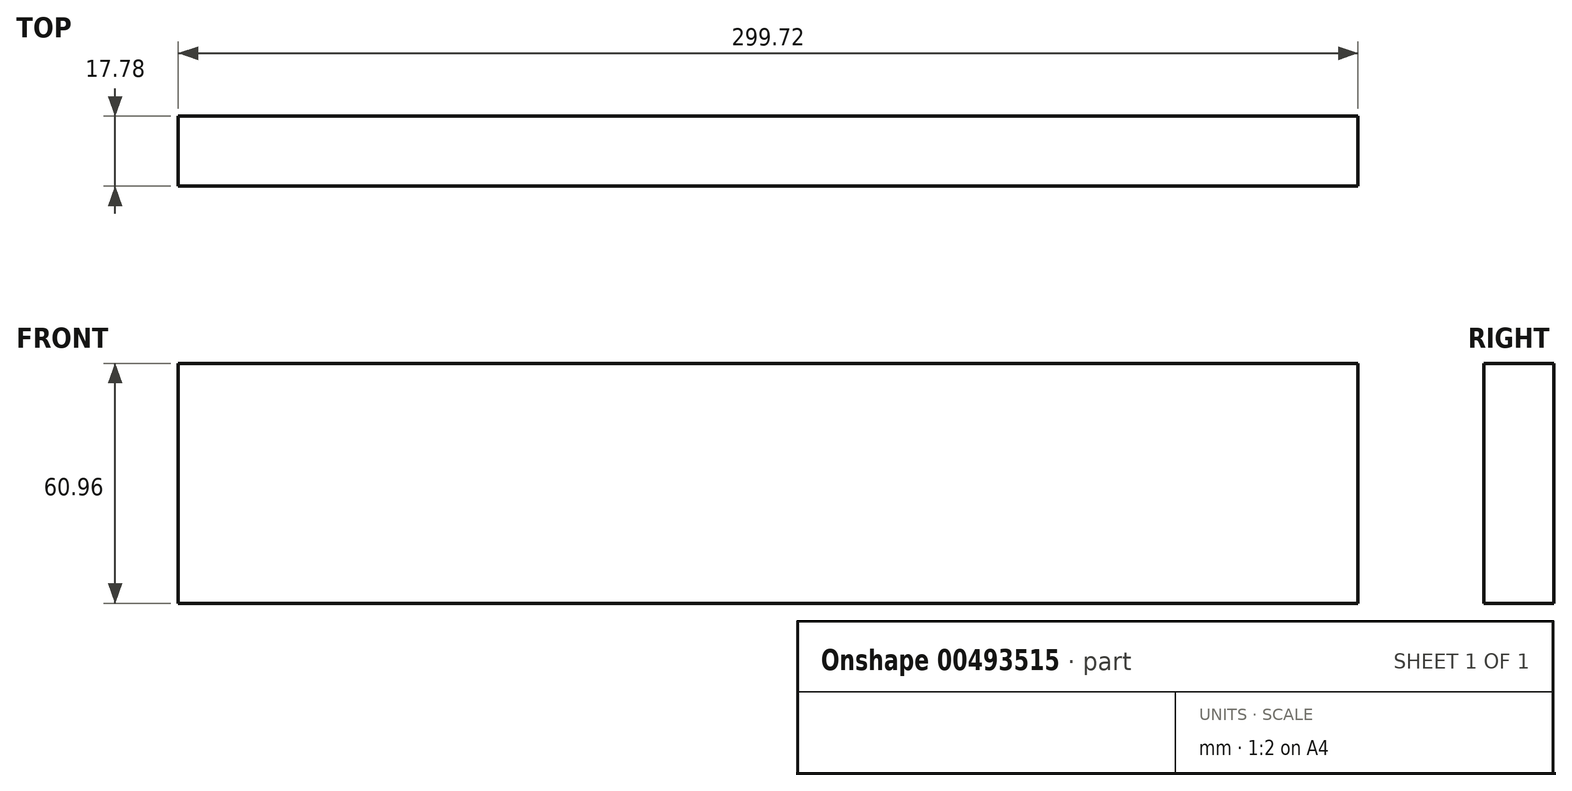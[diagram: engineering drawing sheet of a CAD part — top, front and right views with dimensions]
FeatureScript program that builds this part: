
annotation { "Feature Type Name" : "Feature", "Feature Type Description" : "" }
export const myFeature = defineFeature(function(context is Context, id is Id, definition is map)
    precondition{}
    {
        {
            var Q0;
            Q0=qCreatedBy(makeId("Front.planeOp"),FACE);
            var sketch = newSketch(context, id + "F0", { "sketchPlane" : qUnion([Q0])});
            skLineSegment(sketch, "E0.bottom", {"start": v(-149.05, 19.38) * mm, "end": v(150.67, 19.38) * mm});
            skLineSegment(sketch, "E0.top", {"start": v(-149.05, -41.58) * mm, "end": v(150.67, -41.58) * mm});
            skLineSegment(sketch, "E0.left", {"start": v(-149.05, 19.38) * mm, "end": v(-149.05, -41.58) * mm});
            skLineSegment(sketch, "E0.right", {"start": v(150.67, 19.38) * mm, "end": v(150.67, -41.58) * mm});
            skSolve(sketch);
        }
        {
            var Q0;
            Q0=makeQuery(id+"F0.imprint","IMPRINT",FACE,{"disambiguationData":[TD([[makeQuery(id+"F0.imprint","IMPRINT",EDGE,{"derivedFrom":sQuery(id+"F0.wireOp",EDGE,"E0.bottom")}),-1.0]])]});
            extrude(context, id + "F1", {"entities" : qUnion([Q0]), "depth" : 17.78 * mm});
        }
    });
